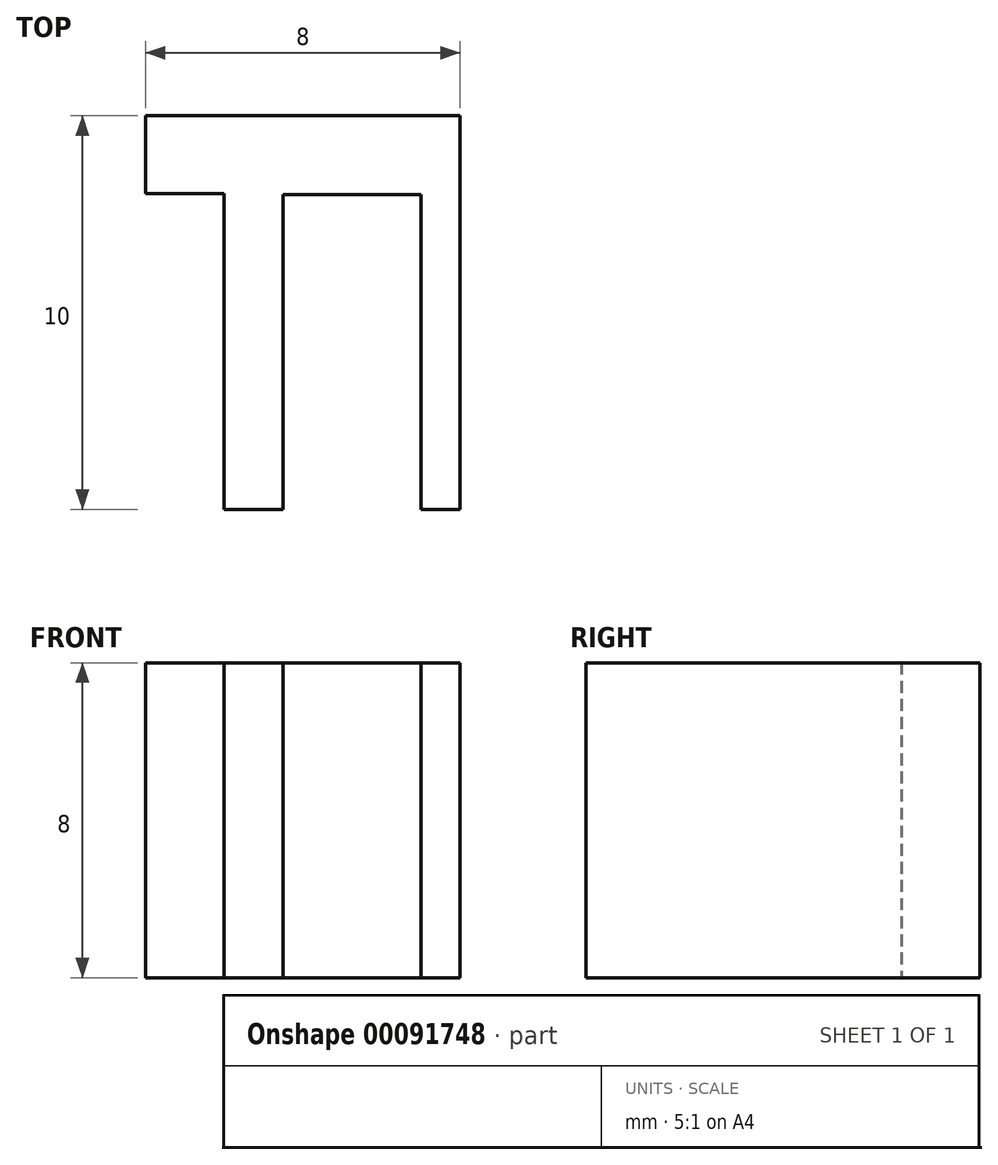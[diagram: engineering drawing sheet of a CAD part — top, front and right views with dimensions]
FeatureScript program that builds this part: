
annotation { "Feature Type Name" : "Feature", "Feature Type Description" : "" }
export const myFeature = defineFeature(function(context is Context, id is Id, definition is map)
    precondition{}
    {
        {
            var Q0;
            Q0=qCreatedBy(makeId("Top.planeOp"),FACE);
            var sketch = newSketch(context, id + "F0", { "sketchPlane" : qUnion([Q0])});
            skPoint(sketch, "E0.middle", {"position": v(0, 0) * mm});
            skLineSegment(sketch, "E1.bottom", {"start": v(3, -5) * mm, "end": v(-3, -5) * mm, "construction": true});
            skLineSegment(sketch, "E1.top", {"start": v(3, 5) * mm, "end": v(-3, 5) * mm, "construction": true});
            skLineSegment(sketch, "E1.left", {"start": v(3, -5) * mm, "end": v(3, 5) * mm, "construction": true});
            skLineSegment(sketch, "E1.right", {"start": v(-3, -5) * mm, "end": v(-3, 5) * mm, "construction": true});
            skLineSegment(sketch, "E2.bottom", {"start": v(-1.5, -5) * mm, "end": v(2, -5) * mm, "construction": true});
            skLineSegment(sketch, "E2.top", {"start": v(-1.5, 3) * mm, "end": v(2, 3) * mm, "construction": true});
            skLineSegment(sketch, "E2.left", {"start": v(-1.5, -5) * mm, "end": v(-1.5, 3) * mm, "construction": true});
            skLineSegment(sketch, "E2.right", {"start": v(2, -5) * mm, "end": v(2, 3) * mm, "construction": true});
            skLineSegment(sketch, "E3", {"start": v(2, -1.74) * mm, "end": v(3, -1.74) * mm, "construction": true});
            skLineSegment(sketch, "E4.bottom", {"start": v(-3, 5) * mm, "end": v(-5, 5) * mm, "construction": true});
            skLineSegment(sketch, "E4.top", {"start": v(-3, 3.03) * mm, "end": v(-5, 3.03) * mm, "construction": true});
            skLineSegment(sketch, "E4.left", {"start": v(-3, 5) * mm, "end": v(-3, 3.03) * mm, "construction": true});
            skLineSegment(sketch, "E4.right", {"start": v(-5, 5) * mm, "end": v(-5, 3.03) * mm, "construction": true});
            skLineSegment(sketch, "E5", {"start": v(-5, 5) * mm, "end": v(3, 5) * mm});
            skLineSegment(sketch, "E6", {"start": v(3, -5) * mm, "end": v(2, -5) * mm});
            skLineSegment(sketch, "E7", {"start": v(2, 3) * mm, "end": v(-1.5, 3) * mm});
            skLineSegment(sketch, "E8", {"start": v(-1.5, -5) * mm, "end": v(-3, -5) * mm});
            skLineSegment(sketch, "E9", {"start": v(-3, 3.03) * mm, "end": v(-5, 3.03) * mm});
            skLineSegment(sketch, "E10", {"start": v(-5, 5) * mm, "end": v(-5, 3.03) * mm});
            skLineSegment(sketch, "E11", {"start": v(-3, 3.03) * mm, "end": v(-3, -5) * mm});
            skLineSegment(sketch, "E12", {"start": v(-1.5, -5) * mm, "end": v(-1.5, 3) * mm});
            skLineSegment(sketch, "E13", {"start": v(2, 3) * mm, "end": v(2, -5) * mm});
            skLineSegment(sketch, "E14", {"start": v(3, -5) * mm, "end": v(3, 5) * mm});
            skSolve(sketch);
        }
        {
            var Q0;
            Q0=makeQuery(id+"F0.imprint","IMPRINT",FACE,{"disambiguationData":[TD([[makeQuery(id+"F0.imprint","IMPRINT",EDGE,{"derivedFrom":sQuery(id+"F0.wireOp",EDGE,"E5")}),-1.0]])]});
            extrude(context, id + "F1", {"entities" : qUnion([Q0]), "depth" : 8 * mm, "symmetric" : true});
        }
    });
